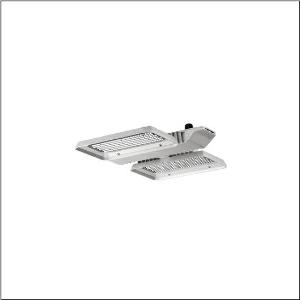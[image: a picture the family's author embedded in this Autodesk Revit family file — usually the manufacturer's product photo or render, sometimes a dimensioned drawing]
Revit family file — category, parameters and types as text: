
# Revit family: highbay_11_51hlasd14fga
name_source: partatom
category: Lighting Fixtures
units: mm (PartAtom-declared; Revit-internal decimal feet)

## family parameters
Cut with Voids When Loaded = No
Host = Face
Light Source = No
Part Type = Normal
Room Calculation Point = No
Round Connector Dimension = Use Diameter
Shared = No

## types (1)
- --- (1 x LED, 14400 lm, 81.3 W, 4000K)
    Apparent Load = 81 VA
    CIE Flux Codes = 89 96 99 100 100
    Color Rendering = 80
    Color Temperature = 4000K
    Default Elevation = 1800 mm
    Description = Highbay 11, LED high bay luminaire, primary light control with lens, of PMMA, light emission: direct distribution, primary light characteristic: symmetric, installation type: suspended mounting, for 1x 2x LED, rated luminous flux: 14.400lm, luminous efficacy: 177lm/W, light colour: 840, colour temperature: 4000K, control gear: ECG DALI, with terminal, 5-pole, max. 2.5mm², mains connection: 230..240V, AC, 50/60Hz, rated input power: 81W, LED unit, of diecast aluminium, unplated, bead blasted, silver, length: 470mm, width: 500mm, height: 65mm, housing, of diecast aluminium, uncoated, bead blasted, silver, protection rating (complete): IP20, insulation class (complete): insulation class I (protective earthing), certification: CE, ENEC, VDE, UKCA, protection symbol: D, ball protection: ball impact resistant according to DIN VDE 0710 part 13 (with chain suspension), permissible operating ambient temperature: -35..+55°C, corresponds to IFS (International Featured Standards) requirements for safety and quality in the food industry, reducing of maximum allowable ambient temperature of 5°C with ceiling mounting, packaging unit: 1 piece
    Height = 95 mm
    Lamp = 1 x LED
    Lamp Light Flux = 14400 lm
    Lamp Power = 81.3 W
    Lamp count = 1
    Length = 468 mm
    Luminous efficacy = 177 lm/W
    Manufacturer = Siteco
    ModVariant = No
    Model = 51HLASD14FGA
    Mounting Place = Ceiling
    Mounting Type = Pendant
    Number of Poles = 1
    OnlyDefault = Yes
    Power Factor = 1
    Product Name = Highbay 11
    Product group = LED high bay luminaire
    ProductGroupID = 903
    Protection Class = Protection class I
    Protection Degree = IP 20
    RLX_Detail_Level = 1
    RLX_Emergency_Light_Flux = 0 lm
    RLX_Emergency_Type = 0
    RLX_Emergency_Type_DB = No
    RlxData = <blob elided: 53717 chars, md5=fcd40f07>
    Socket = socket
    Standby Power = 0 W
    System Light Flux = 14400 lm
    System Power = 81 W
    Type Comments = factory setting: luminous flux: 100 % | dim-lin: 254 | 460 mA
    Type Image = l_1006019.jpg
    URL = http://relux.com
    VarID = @adj_158285
    Voltage = 0 V
    Weight = 0.00 kg
    Width = 501 mm

## geometry (parser evidence)
native form markers: Blend x4, Sweep x15
no freeform markers — native parametric forms only
